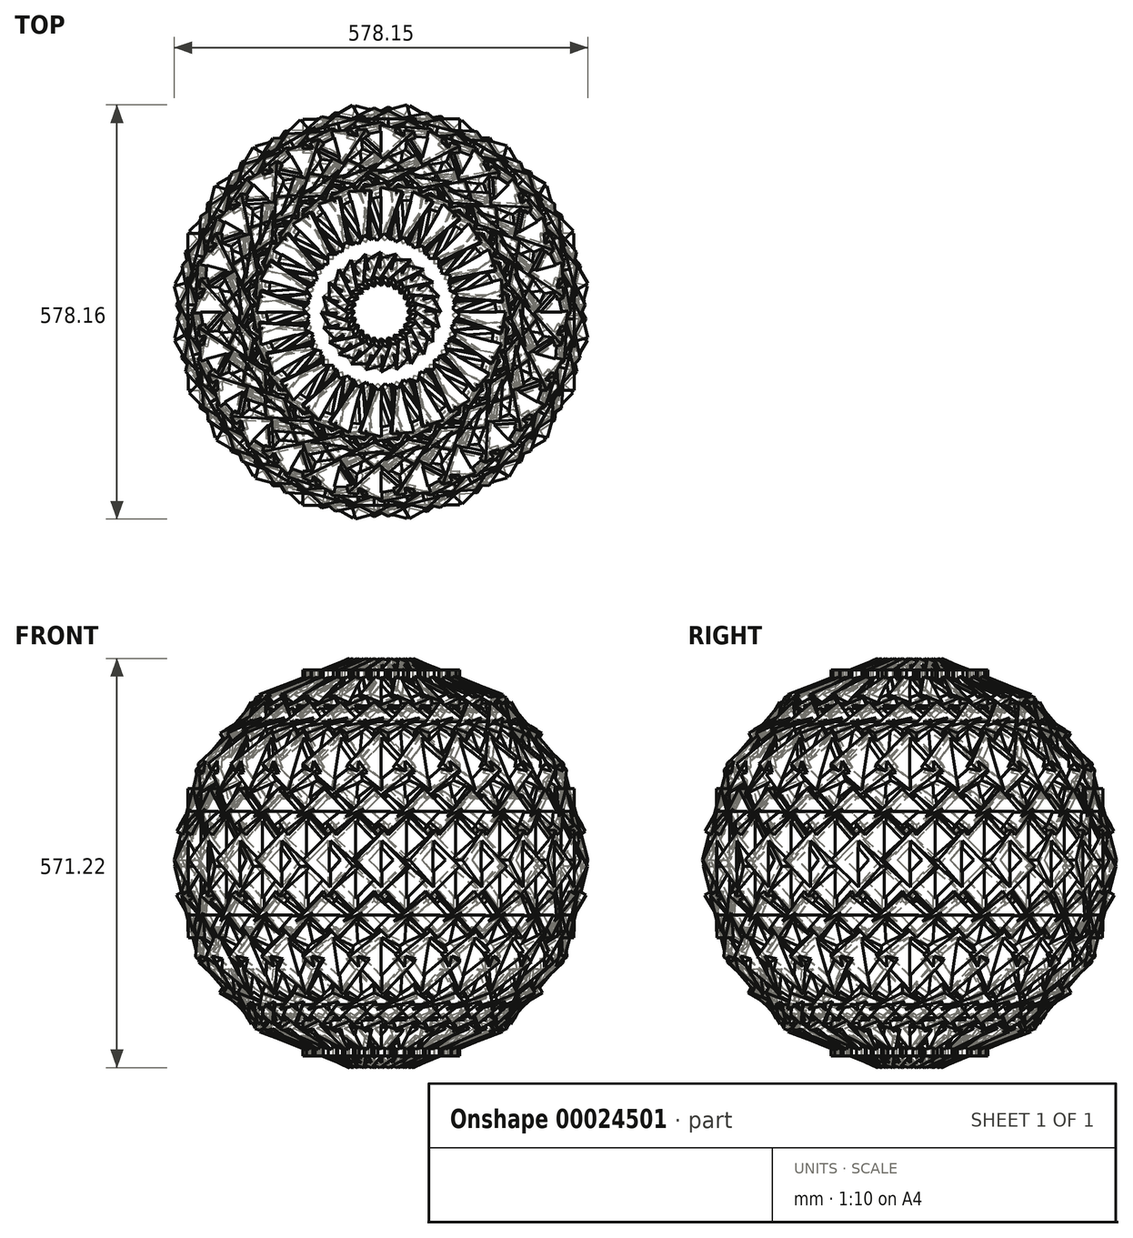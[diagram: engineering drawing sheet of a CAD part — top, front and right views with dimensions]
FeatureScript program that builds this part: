
annotation { "Feature Type Name" : "Feature", "Feature Type Description" : "" }
export const myFeature = defineFeature(function(context is Context, id is Id, definition is map)
    precondition{}
    {
        {
            var Q0;
            Q0=qCreatedBy(makeId("Top.planeOp"),FACE);
            var sketch = newSketch(context, id + "F0", { "sketchPlane" : qUnion([Q0])});
            skLineSegment(sketch, "E0", {"start": v(0, 0) * mm, "end": v(534.4, 0) * mm});
            skCircle(sketch, "E1", {"center": v(267.2, 0) * mm, "radius": 267.2 * mm});
            skSolve(sketch);
        }
        {
            var Q0;
            Q0=qCreatedBy(makeId("Top.planeOp"),FACE);
            var sketch = newSketch(context, id + "F1", { "sketchPlane" : qUnion([Q0])});
            skLineSegment(sketch, "E2", {"start": v(271.48, 109.55) * mm, "end": v(171.78, 9.86) * mm});
            skLineSegment(sketch, "E3", {"start": v(171.78, 9.86) * mm, "end": v(271.48, -89.84) * mm});
            skLineSegment(sketch, "E4", {"start": v(271.48, 109.55) * mm, "end": v(371.17, 9.86) * mm});
            skLineSegment(sketch, "E5", {"start": v(271.48, -89.84) * mm, "end": v(371.17, 9.86) * mm});
            skSolve(sketch);
        }
        {
            var Q0;
            Q0 = qSketchRegion(id + "F1", true);
            extrude(context, id + "F2", {"entities" : qUnion([Q0]), "offsetDistance" : 25.4 * mm, "depth" : 279.4 * mm});
        }
        {
            var Q0;
            Q0=qCreatedBy(makeId("Front.planeOp"),FACE);
            var sketch = newSketch(context, id + "F3", { "sketchPlane" : qUnion([Q0])});
            skCircle(sketch, "E6", {"center": v(266.85, 9.84) * mm, "radius": 230.79 * mm});
            skSolve(sketch);
        }
        {
            var Q0;
            Q0=makeQuery(id+"F2.opExtrude","SWEPT_BODY",BODY,{"disambiguationData":[OSD([sQuery(id+"F1.wireOp",EDGE,"E2"),sQuery(id+"F1.wireOp",EDGE,"E3"),sQuery(id+"F1.wireOp",EDGE,"E4"),sQuery(id+"F1.wireOp",EDGE,"E5")])]});
            var Q1;
            Q1=sQuery(id+"F3.wireOp",EDGE,"E6");
            circularPattern(context, id + "F4", {"operationType" : NewBodyOperationType.ADD, "entities" : qUnion([Q0]), "axis" : qUnion([Q1]), "angle" : 30 * degree, "instanceCount" : 12});
        }
        {
            var Q0;
            Q0=makeQuery(id+"F2.opExtrude","SWEPT_BODY",BODY,{"disambiguationData":[OSD([sQuery(id+"F1.wireOp",EDGE,"E2"),sQuery(id+"F1.wireOp",EDGE,"E3"),sQuery(id+"F1.wireOp",EDGE,"E4"),sQuery(id+"F1.wireOp",EDGE,"E5")])]});
            var Q1;
            Q1=sQuery(id+"F0.wireOp",EDGE,"E1");
            circularPattern(context, id + "F5", {"operationType" : NewBodyOperationType.ADD, "entities" : qUnion([Q0]), "axis" : qUnion([Q1]), "angle" : 15 * degree, "instanceCount" : 24});
        }
    });
